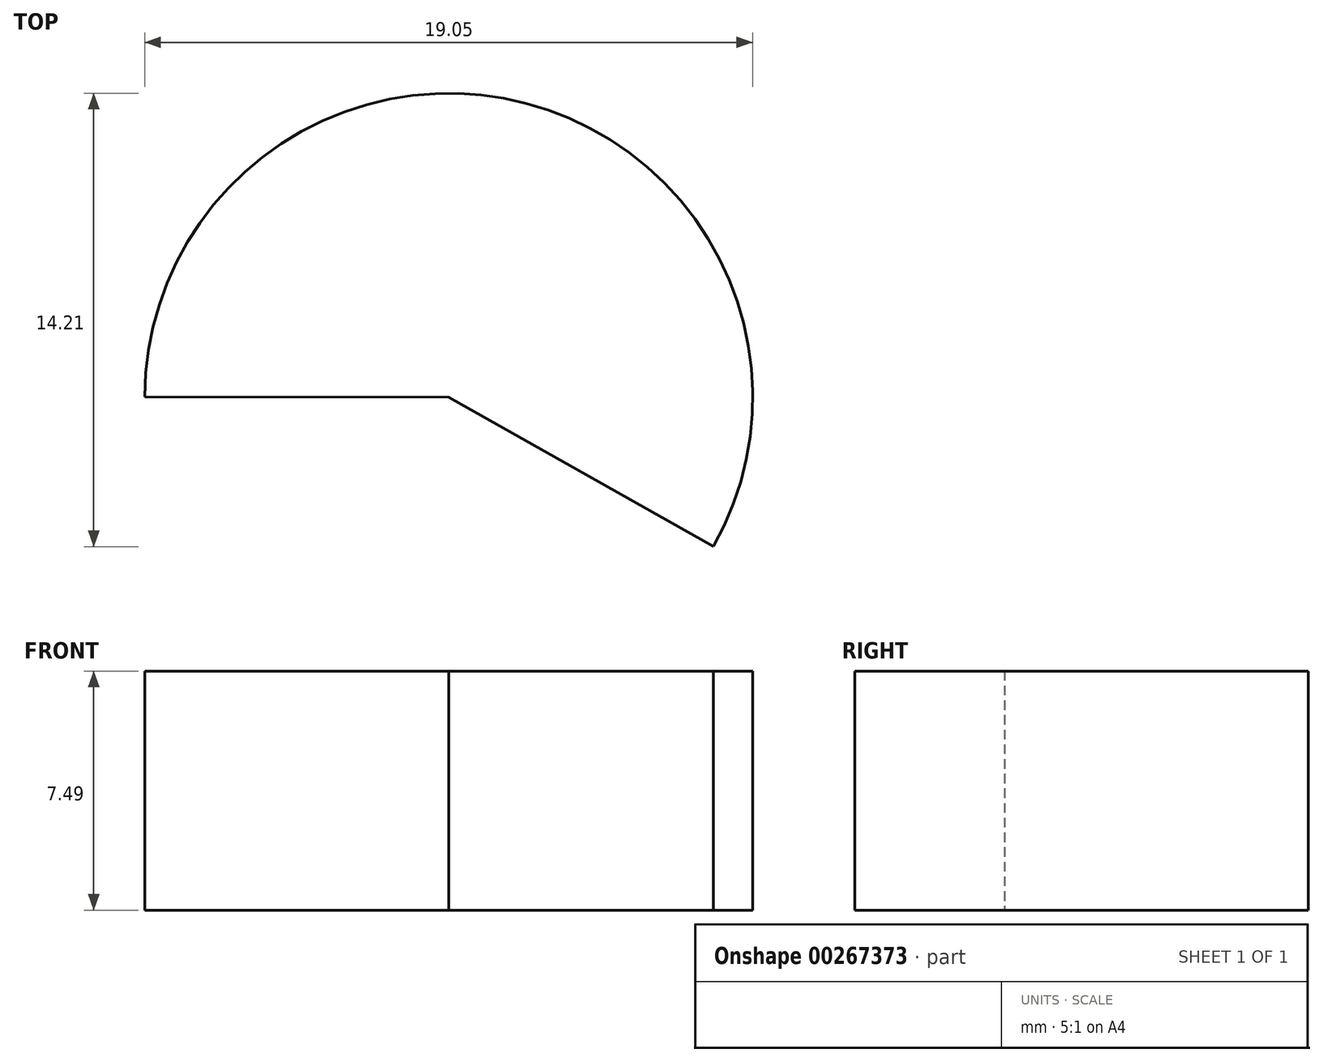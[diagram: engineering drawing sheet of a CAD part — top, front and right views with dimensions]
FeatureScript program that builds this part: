
annotation { "Feature Type Name" : "Feature", "Feature Type Description" : "" }
export const myFeature = defineFeature(function(context is Context, id is Id, definition is map)
    precondition{}
    {
        {
            var Q0;
            Q0=qCreatedBy(makeId("Top.planeOp"),FACE);
            var sketch = newSketch(context, id + "F0", { "sketchPlane" : qUnion([Q0])});
            skArc(sketch, "E0", {"start": v(-16.78, 16.5) * mm, "mid": v(-22.65, 30.4) * mm, "end": v(-34.6, 21.2) * mm});
            skLineSegment(sketch, "E1", {"start": v(-34.6, 21.2) * mm, "end": v(-25.07, 21.18) * mm});
            skLineSegment(sketch, "E2", {"start": v(-25.07, 21.18) * mm, "end": v(-16.78, 16.5) * mm});
            skSolve(sketch);
        }
        {
            var Q0;
            Q0=makeQuery(id+"F0.imprint","IMPRINT",FACE,{"disambiguationData":[TD([[makeQuery(id+"F0.imprint","IMPRINT",EDGE,{"derivedFrom":sQuery(id+"F0.wireOp",EDGE,"E0")}),1.0]])]});
            extrude(context, id + "F1", {"entities" : qUnion([Q0]), "depth" : 7.5 * mm});
        }
    });
